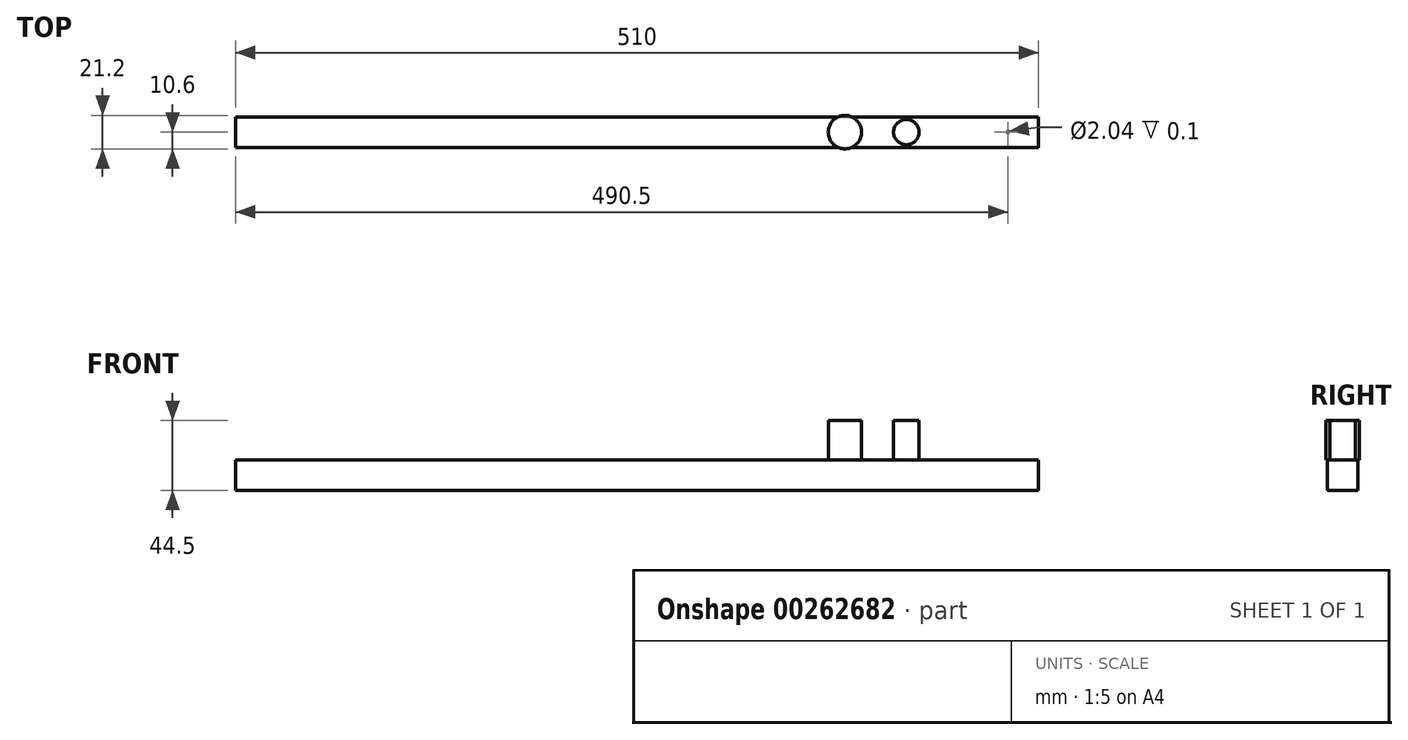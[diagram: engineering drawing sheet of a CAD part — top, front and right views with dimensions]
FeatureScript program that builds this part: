
annotation { "Feature Type Name" : "Feature", "Feature Type Description" : "" }
export const myFeature = defineFeature(function(context is Context, id is Id, definition is map)
    precondition{}
    {
        {
            var Q0;
            Q0=qCreatedBy(makeId("Right.planeOp"),FACE);
            var sketch = newSketch(context, id + "F0", { "sketchPlane" : qUnion([Q0])});
            skLineSegment(sketch, "E0.bottom", {"start": v(-9.7, -9.7) * mm, "end": v(9.7, -9.7) * mm});
            skLineSegment(sketch, "E0.top", {"start": v(-9.7, 9.7) * mm, "end": v(9.7, 9.7) * mm});
            skLineSegment(sketch, "E0.left", {"start": v(-9.7, -9.7) * mm, "end": v(-9.7, 9.7) * mm});
            skLineSegment(sketch, "E0.right", {"start": v(9.7, -9.7) * mm, "end": v(9.7, 9.7) * mm});
            skPoint(sketch, "E0.middle", {"position": v(0, 0) * mm});
            skSolve(sketch);
        }
        {
            var Q0;
            Q0 = qSketchRegion(id + "F0", true);
            extrude(context, id + "F1", {"entities" : qUnion([Q0]), "oppositeDirection" : true, "depth" : 510 * mm});
        }
        {
            var Q0;
            Q0=makeQuery(id+"F1.opExtrude","SWEPT_FACE",FACE,{"disambiguationData":[OSD([sQuery(id+"F0.wireOp",EDGE,"E0.top")])]});
            cPlane(context, id + "F2", {"entities" : qUnion([Q0]), "cplaneType" : CPlaneType.OFFSET, "offset" : 0 * mm, "width" : 150 * mm, "height" : 150 * mm});
        }
        {
            var Q0;
            Q0=qCreatedBy(id+"F2.planeOp",FACE);
            var sketch = newSketch(context, id + "F3", { "sketchPlane" : qUnion([Q0])});
            skCircle(sketch, "E1", {"center": v(-42, 0) * mm, "radius": 5 * mm});
            skCircle(sketch, "E2", {"center": v(-257, 0) * mm, "radius": 5 * mm});
            skCircle(sketch, "E3", {"center": v(-364.5, 0) * mm, "radius": 5 * mm});
            skCircle(sketch, "E4", {"center": v(-472, 0) * mm, "radius": 5 * mm});
            skCircle(sketch, "E5", {"center": v(-84, 0) * mm, "radius": 8.05 * mm});
            skCircle(sketch, "E6", {"center": v(-123, 0) * mm, "radius": 10.6 * mm});
            skCircle(sketch, "E7", {"center": v(-27, 0) * mm, "radius": 3.3 * mm});
            skSolve(sketch);
        }
        {
            var Q0;
            Q0=makeQuery(id+"F3.imprint","IMPRINT",FACE,{"disambiguationData":[TD([[makeQuery(id+"F3.imprint","IMPRINT",EDGE,{"derivedFrom":sQuery(id+"F3.wireOp",EDGE,"E6")}),1.0]])]});
            var Q1;
            Q1=makeQuery(id+"F3.imprint","IMPRINT",FACE,{"disambiguationData":[TD([[makeQuery(id+"F3.imprint","IMPRINT",EDGE,{"derivedFrom":sQuery(id+"F3.wireOp",EDGE,"E5")}),1.0]])]});
            extrude(context, id + "F4", {"entities" : qUnion([Q0, Q1]), "operationType" : NewBodyOperationType.ADD, "depth" : 25 * mm});
        }
        {
            var Q0;
            Q0=sQuery(id+"F3.wireOp",EDGE,"E4");
            var Q1;
            Q1=sQuery(id+"F3.wireOp",EDGE,"E3");
            var Q2;
            Q2=sQuery(id+"F3.wireOp",EDGE,"E2");
            var Q3;
            Q3=sQuery(id+"F3.wireOp",EDGE,"E1");
            var Q4;
            Q4=sQuery(id+"F3.wireOp",EDGE,"E7");
            extrude(context, id + "F5", {"bodyType" : ToolBodyType.SURFACE, "surfaceEntities" : qUnion([Q0, Q1, Q2, Q3, Q4]), "depth" : .1 * mm});
        }
        {
            var Q0;
            Q0=makeQuery(id+"F1.opExtrude","SWEPT_FACE",FACE,{"disambiguationData":[OSD([sQuery(id+"F0.wireOp",EDGE,"E0.bottom")])]});
            cPlane(context, id + "F6", {"entities" : qUnion([Q0]), "cplaneType" : CPlaneType.OFFSET, "offset" : 0 * mm, "width" : 150 * mm, "height" : 150 * mm});
        }
        {
            var Q0;
            Q0=qCreatedBy(id+"F6.planeOp",FACE);
            var sketch = newSketch(context, id + "F7", { "sketchPlane" : qUnion([Q0])});
            skLineSegment(sketch, "E8.0.0", {"start": v(0, -9.7) * mm, "end": v(0, 9.7) * mm});
            skLineSegment(sketch, "E8.0.1", {"start": v(0, 9.7) * mm, "end": v(-510, 9.7) * mm});
            skLineSegment(sketch, "E8.0.2", {"start": v(-510, 9.7) * mm, "end": v(-510, -9.7) * mm});
            skLineSegment(sketch, "E8.0.3", {"start": v(-510, -9.7) * mm, "end": v(0, -9.7) * mm});
            skCircle(sketch, "E9", {"center": v(-19.5, 0) * mm, "radius": 1.02 * mm});
            skPoint(sketch, "E9.centerSnap0", {"position": v(0, 0) * mm});
            skCircle(sketch, "E10.0", {"center": v(-27, 0) * mm, "radius": 3.3 * mm, "construction": true});
            skSolve(sketch);
        }
        {
            var Q0;
            Q0 = qSketchRegion(id + "F7", true);
            extrude(context, id + "F8", {"entities" : qUnion([Q0]), "operationType" : NewBodyOperationType.ADD, "depth" : .1 * mm});
        }
    });
